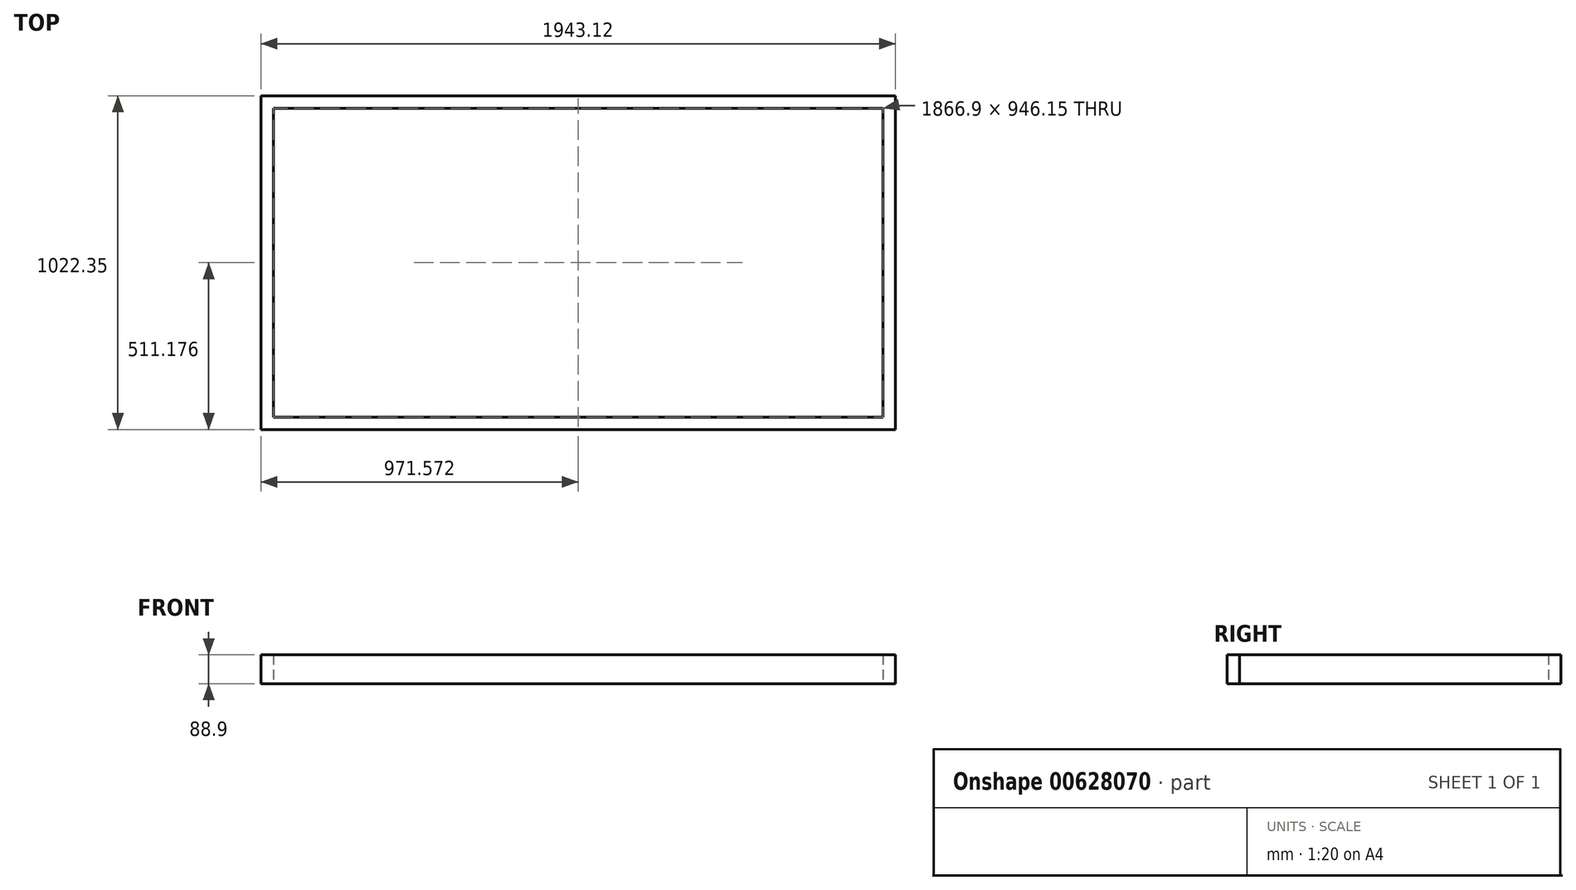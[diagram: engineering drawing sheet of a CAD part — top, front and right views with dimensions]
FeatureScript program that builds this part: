
annotation { "Feature Type Name" : "Feature", "Feature Type Description" : "" }
export const myFeature = defineFeature(function(context is Context, id is Id, definition is map)
    precondition{}
    {
        {
            var Q0;
            Q0=qCreatedBy(makeId("Top.planeOp"),FACE);
            var sketch = newSketch(context, id + "F0", { "sketchPlane" : qUnion([Q0])});
            skLineSegment(sketch, "E0.bottom", {"start": v(-980.33, 6.9) * mm, "end": v(962.77, 6.9) * mm});
            skLineSegment(sketch, "E0.top", {"start": v(-980.33, -31.2) * mm, "end": v(962.77, -31.2) * mm});
            skLineSegment(sketch, "E0.left", {"start": v(-980.33, 6.9) * mm, "end": v(-980.33, -31.2) * mm});
            skLineSegment(sketch, "E0.right", {"start": v(962.77, 6.9) * mm, "end": v(962.77, -31.2) * mm});
            skLineSegment(sketch, "E1.bottom", {"start": v(-980.35, -977.36) * mm, "end": v(962.75, -977.36) * mm});
            skLineSegment(sketch, "E1.top", {"start": v(-980.35, -1015.46) * mm, "end": v(962.75, -1015.46) * mm});
            skLineSegment(sketch, "E1.left", {"start": v(-980.35, -977.36) * mm, "end": v(-980.35, -1015.46) * mm});
            skLineSegment(sketch, "E1.right", {"start": v(962.75, -977.36) * mm, "end": v(962.75, -1015.46) * mm});
            skLineSegment(sketch, "E2.bottom", {"start": v(-980.33, -31.2) * mm, "end": v(-942.23, -31.2) * mm});
            skLineSegment(sketch, "E2.top", {"start": v(-980.33, -977.36) * mm, "end": v(-942.23, -977.36) * mm});
            skLineSegment(sketch, "E2.left", {"start": v(-980.33, -31.2) * mm, "end": v(-980.33, -977.36) * mm});
            skLineSegment(sketch, "E2.right", {"start": v(-942.23, -31.2) * mm, "end": v(-942.23, -977.36) * mm});
            skLineSegment(sketch, "E3.bottom", {"start": v(962.77, -31.2) * mm, "end": v(924.67, -31.2) * mm});
            skLineSegment(sketch, "E3.top", {"start": v(962.77, -977.36) * mm, "end": v(924.67, -977.36) * mm});
            skLineSegment(sketch, "E3.left", {"start": v(962.77, -31.2) * mm, "end": v(962.77, -977.36) * mm});
            skLineSegment(sketch, "E3.right", {"start": v(924.67, -31.2) * mm, "end": v(924.67, -977.36) * mm});
            skLineSegment(sketch, "E4.bottom", {"start": v(-504.08, -31.2) * mm, "end": v(-465.98, -31.2) * mm});
            skLineSegment(sketch, "E4.top", {"start": v(-504.08, -977.36) * mm, "end": v(-465.98, -977.36) * mm});
            skLineSegment(sketch, "E4.left", {"start": v(-504.08, -31.2) * mm, "end": v(-504.08, -977.36) * mm});
            skLineSegment(sketch, "E4.right", {"start": v(-465.98, -31.2) * mm, "end": v(-465.98, -977.36) * mm});
            skLineSegment(sketch, "E5.bottom", {"start": v(-27.83, -31.2) * mm, "end": v(10.27, -31.2) * mm});
            skLineSegment(sketch, "E5.top", {"start": v(-27.83, -977.36) * mm, "end": v(10.27, -977.36) * mm});
            skLineSegment(sketch, "E5.left", {"start": v(-27.83, -31.2) * mm, "end": v(-27.83, -977.36) * mm});
            skLineSegment(sketch, "E5.right", {"start": v(10.27, -31.2) * mm, "end": v(10.27, -977.36) * mm});
            skLineSegment(sketch, "E6.bottom", {"start": v(448.42, -31.2) * mm, "end": v(486.52, -31.2) * mm});
            skLineSegment(sketch, "E6.top", {"start": v(448.42, -977.36) * mm, "end": v(486.52, -977.36) * mm});
            skLineSegment(sketch, "E6.left", {"start": v(448.42, -31.2) * mm, "end": v(448.42, -977.36) * mm});
            skLineSegment(sketch, "E6.right", {"start": v(486.52, -31.2) * mm, "end": v(486.52, -977.36) * mm});
            skSolve(sketch);
        }
        {
            var Q0;
            Q0 = qSketchRegion(id + "F0", true);
            var Q1;
            Q1=makeQuery(id+"F0.imprint","IMPRINT",FACE,{"disambiguationData":[TD([[makeQuery(id+"F0.imprint","IMPRINT",EDGE,{"derivedFrom":sQuery(id+"F0.wireOp",EDGE,"E4.bottom")}),-1.0]])]});
            var Q2;
            Q2=makeQuery(id+"F0.imprint","IMPRINT",FACE,{"disambiguationData":[TD([[makeQuery(id+"F0.imprint","IMPRINT",EDGE,{"derivedFrom":sQuery(id+"F0.wireOp",EDGE,"E5.bottom")}),-1.0]])]});
            var Q3;
            Q3=makeQuery(id+"F0.imprint","IMPRINT",FACE,{"disambiguationData":[TD([[makeQuery(id+"F0.imprint","IMPRINT",EDGE,{"derivedFrom":sQuery(id+"F0.wireOp",EDGE,"E6.bottom")}),-1.0]])]});
            extrude(context, id + "F1", {"entities" : qUnion([Q0, Q1, Q2, Q3]), "depth" : 88.9 * mm, "offsetDistance" : 25.4 * mm});
        }
    });
